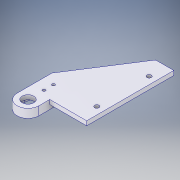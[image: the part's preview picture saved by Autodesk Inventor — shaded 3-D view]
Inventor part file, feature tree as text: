
AUTODESK INVENTOR PART (.ipt)
format: ipt  version: 2017 (Build 210142000, 142)  size: 154,624 bytes
history: native  units: in
note: dims shown in document units (in); Inventor stores cm internally (conversion verified against a paired STEP export)
features: extrude x2, sketch x2, projected_geometry x1
ambient origin geometry x8: Origin, YZ Plane, XZ Plane, XY Plane, X Axis, Y Axis, Z Axis, Center Point
bodies: Solid1 (feature_tree)
feature tree (5):
  extrude  "Extrusion1"  TaperAngle=90.0deg  [1 undecoded]
  extrude  "Extrusion3"  Depth=1.0in
  sketch  "Sketch3"  dims[d6=2.3622in d7=90.0deg]
  sketch  "Sketch6"  dims[d8=0.4929in d9=1.0in d10=0.2953in d11=0.5906in d13=0.9456in d14=0.1181in d15=0.0in d18=0.1969in d19=0.4724in d20=0.4724in d21=0.1181in d22=0.1181in d25=0.315in d26=0.4335in d27=0.2562in d28=0.0787in d29=0.0787in d31=0.4331in d32=0.0591in d33=0.2362in d34=0.1181in d35=0.2362in d36=0.0in]
  projected_geometry  "Projected Loop3"
note: 1 required parameter value undecoded (feature->parameter linkage not recoverable at this tier; creation-order binding heuristic only, values carry confidence <= 0.55)
